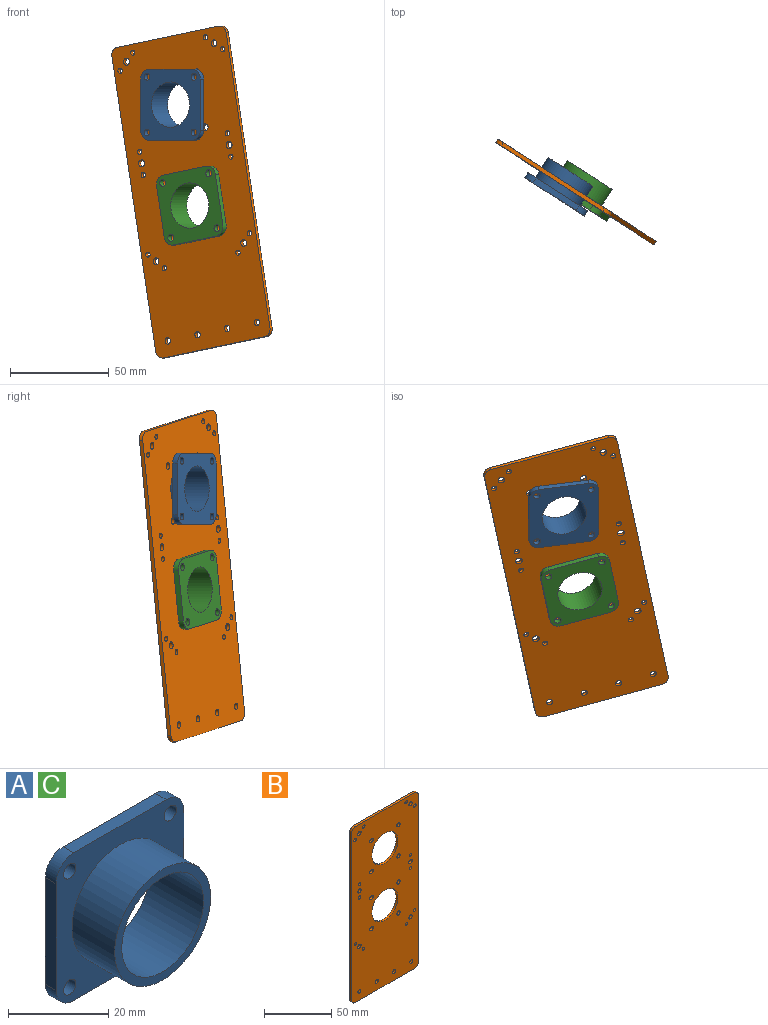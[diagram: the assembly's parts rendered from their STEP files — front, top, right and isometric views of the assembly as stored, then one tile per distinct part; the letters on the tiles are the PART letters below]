
ASSEMBLY  parts=3 mates=2
PART A: 17 faces, bbox 36x15x36 mm
  f0: cylinder r=11.5mm len=23mm, axis (0,1,0), area 1083.8mm2, adj f2,f3
  f1: cylinder r=13.5mm len=27mm, axis (0,1,0), area 1017.9mm2, adj f2,f12
  f2: plane 27x27mm, normal (0,-1,0), area 157.1mm2, adj f0,f1
  f3: plane 36x36mm, normal (0,1,0), area 820.6mm2, adj f0,f4,f5,f6,f7,f8,f9,f10
  f4: plane 26x3mm, normal (-1,0,0), area 78mm2, adj f3,f12,f13,f16
  f5: plane 26x3mm, normal (0,0,-1), area 78mm2, adj f3,f12,f13,f14
  f6: plane 26x3mm, normal (1,0,0), area 78mm2, adj f3,f12,f14,f15
  f7: cylinder r=1.75mm len=3.5mm, axis (0,1,0), area 33mm2, adj f3,f12
  f8: cylinder r=1.75mm len=3.5mm, axis (0,1,0), area 33mm2, adj f3,f12
  f9: cylinder r=1.75mm len=3.5mm, axis (0,1,0), area 33mm2, adj f3,f12
  f10: cylinder r=1.75mm len=3.5mm, axis (0,1,0), area 33mm2, adj f3,f12
  f11: plane 26x3mm, normal (0,0,1), area 78mm2, adj f3,f12,f15,f16
  f12: plane 36x36mm, normal (0,-1,0), area 663.5mm2, adj f1,f4,f5,f6,f7,f8,f9,f10
  f13: cylinder r=5mm len=5mm, axis (0,1,0), area 23.6mm2, adj f3,f4,f5,f12
  f14: cylinder r=5mm len=5mm, axis (0,-1,0), area 23.6mm2, adj f3,f5,f6,f12
  f15: cylinder r=5mm len=5mm, axis (0,1,0), area 23.6mm2, adj f3,f6,f11,f12
  f16: cylinder r=5mm len=5mm, axis (0,-1,0), area 23.6mm2, adj f3,f4,f11,f12
PART B: 42 faces, bbox 70x2x160 mm
  f0: plane 62x2mm, normal (0,0,1), area 124mm2, adj f36,f37,f38,f41
  f1: plane 152x2mm, normal (-1,0,0), area 304mm2, adj f36,f37,f38,f39
  f2: plane 62x2mm, normal (0,0,-1), area 124mm2, adj f36,f37,f39,f40
  f3: cylinder r=1.3mm len=2.6mm, axis (0,1,0), area 16.3mm2, adj f36,f37
  f4: cylinder r=1.3mm len=2.6mm, axis (0,1,0), area 16.3mm2, adj f36,f37
  f5: cylinder r=1.3mm len=2.6mm, axis (0,1,0), area 16.3mm2, adj f36,f37
  f6: cylinder r=1.75mm len=3.5mm, axis (0,1,0), area 22mm2, adj f36,f37
  f7: cylinder r=1.75mm len=3.5mm, axis (0,1,0), area 22mm2, adj f36,f37
  f8: cylinder r=1.3mm len=2.6mm, axis (0,1,0), area 16.3mm2, adj f36,f37
  f9: cylinder r=1.3mm len=2.6mm, axis (0,1,0), area 16.3mm2, adj f36,f37
  f10: cylinder r=1.3mm len=2.6mm, axis (0,1,0), area 16.3mm2, adj f36,f37
  f11: cylinder r=1.3mm len=2.6mm, axis (0,1,0), area 16.3mm2, adj f36,f37
  f12: cylinder r=1.75mm len=3.5mm, axis (0,1,0), area 22mm2, adj f36,f37
  f13: cylinder r=1.75mm len=3.5mm, axis (0,1,0), area 22mm2, adj f36,f37
  f14: cylinder r=13.65mm len=27.3mm, axis (0,1,0), area 171.5mm2, adj f36,f37
  f15: cylinder r=1.75mm len=3.5mm, axis (0,1,0), area 22mm2, adj f36,f37
  f16: cylinder r=1.75mm len=3.5mm, axis (0,1,0), area 22mm2, adj f36,f37
  f17: cylinder r=1.3mm len=2.6mm, axis (0,1,0), area 16.3mm2, adj f36,f37
  f18: cylinder r=1.3mm len=2.6mm, axis (0,1,0), area 16.3mm2, adj f36,f37
  f19: cylinder r=1.6mm len=3.2mm, axis (0,1,0), area 20.1mm2, adj f36,f37
  f20: cylinder r=1.6mm len=3.2mm, axis (0,1,0), area 20.1mm2, adj f36,f37
  f21: cylinder r=1.6mm len=3.2mm, axis (0,1,0), area 20.1mm2, adj f36,f37
  f22: cylinder r=1.6mm len=3.2mm, axis (0,1,0), area 20.1mm2, adj f36,f37
  f23: cylinder r=1.3mm len=2.6mm, axis (0,1,0), area 16.3mm2, adj f36,f37
  f24: cylinder r=1.3mm len=2.6mm, axis (0,1,0), area 16.3mm2, adj f36,f37
  f25: cylinder r=1.75mm len=3.5mm, axis (0,1,0), area 22mm2, adj f36,f37
  f26: cylinder r=13.65mm len=27.3mm, axis (0,1,0), area 171.5mm2, adj f36,f37
  f27: cylinder r=1.75mm len=3.5mm, axis (0,1,0), area 22mm2, adj f36,f37
  f28: cylinder r=1.75mm len=3.5mm, axis (0,1,0), area 22mm2, adj f36,f37
  f29: cylinder r=1.75mm len=3.5mm, axis (0,1,0), area 22mm2, adj f36,f37
  f30: cylinder r=1.75mm len=3.5mm, axis (0,1,0), area 22mm2, adj f36,f37
  f31: cylinder r=1.75mm len=3.5mm, axis (0,1,0), area 22mm2, adj f36,f37
  f32: cylinder r=1.75mm len=3.5mm, axis (0,1,0), area 22mm2, adj f36,f37
  f33: cylinder r=1.75mm len=3.5mm, axis (0,1,0), area 22mm2, adj f36,f37
  f34: plane 152x2mm, normal (1,0,0), area 304mm2, adj f36,f37,f40,f41
  f35: cylinder r=1.3mm len=2.6mm, axis (0,1,0), area 16.3mm2, adj f36,f37
  f36: plane 160x70mm, normal (0,-1,0), area 9785mm2, adj f0,f1,f2,f3,f4,f5,f6,f7
  f37: plane 160x70mm, normal (0,1,0), area 9785mm2, adj f0,f1,f2,f3,f4,f5,f6,f7
  f38: cylinder r=4mm len=4mm, axis (0,1,0), area 12.6mm2, adj f0,f1,f36,f37
  f39: cylinder r=4mm len=4mm, axis (0,1,0), area 12.6mm2, adj f1,f2,f36,f37
  f40: cylinder r=4mm len=4mm, axis (0,1,0), area 12.6mm2, adj f2,f34,f36,f37
  f41: cylinder r=4mm len=4mm, axis (0,1,0), area 12.6mm2, adj f0,f34,f36,f37
PART C: same geometry as A
PLACE A rot(axis=(0,0,1),147.2deg) t=(-190.25,-48.12,9.02)mm
PLACE B rot(axis=(-0.08,-0.28,-0.96),34.2deg) t=(-185.38,-40.56,9.02)mm
PLACE C rot(axis=(0.96,-0.28,0.08),177.2deg) t=(-180.5,-49.65,-42.19)mm
MATE slider C.f0 <-> B.f14  axis (0.54,0.84,0) through (-178.87,-47.13,-42.19)mm
MATE cylindrical B.f26 <-> A.f0  axis (0.54,0.84,0) through (-185.38,-40.56,9.02)mm
